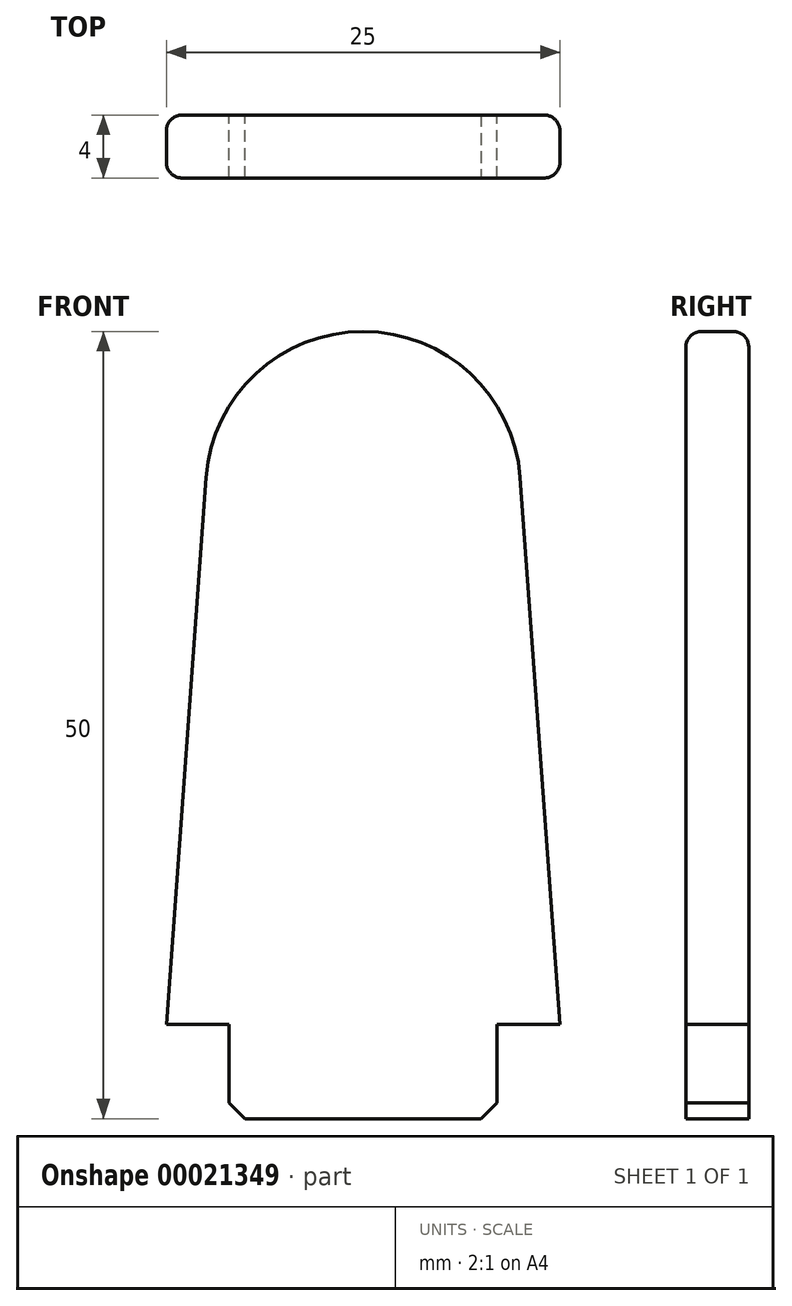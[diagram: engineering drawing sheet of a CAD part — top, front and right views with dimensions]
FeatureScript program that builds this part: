
annotation { "Feature Type Name" : "Feature", "Feature Type Description" : "" }
export const myFeature = defineFeature(function(context is Context, id is Id, definition is map)
    precondition{}
    {
        {
            var Q0;
            Q0=qCreatedBy(makeId("Front.planeOp"),FACE);
            var sketch = newSketch(context, id + "F0", { "sketchPlane" : qUnion([Q0])});
            skLineSegment(sketch, "E0", {"start": v(0, 0) * mm, "end": v(0, 50) * mm});
            skLineSegment(sketch, "E1", {"start": v(0, 0) * mm, "end": v(8.5, 0) * mm});
            skLineSegment(sketch, "E2", {"start": v(8.5, 0) * mm, "end": v(8.5, 6) * mm});
            skLineSegment(sketch, "E3", {"start": v(8.5, 6) * mm, "end": v(12.5, 6) * mm});
            skLineSegment(sketch, "E4", {"start": v(12.5, 6) * mm, "end": v(9.97, 40.73) * mm});
            skArc(sketch, "E5", {"start": v(9.97, 40.73) * mm, "mid": v(6.8, 47.32) * mm, "end": v(0, 50) * mm});
            skLineSegment(sketch, "E6", {"start": v(0, 50) * mm, "end": v(-4.24, 50) * mm});
            skArc(sketch, "E7.MirrorCS", {"start": v(-9.97, 40.73) * mm, "mid": v(-6.8, 47.32) * mm, "end": v(0, 50) * mm});
            skLineSegment(sketch, "E8.MirrorCS", {"start": v(-12.5, 6) * mm, "end": v(-9.97, 40.73) * mm});
            skLineSegment(sketch, "E9.MirrorCS", {"start": v(-8.5, 6) * mm, "end": v(-12.5, 6) * mm});
            skLineSegment(sketch, "E10.MirrorCS", {"start": v(-8.5, 0) * mm, "end": v(-8.5, 6) * mm});
            skLineSegment(sketch, "E11.MirrorCS", {"start": v(0, 0) * mm, "end": v(-8.5, 0) * mm});
            skSolve(sketch);
        }
        {
            var Q0;
            Q0=makeQuery(id+"F0.imprint","IMPRINT",FACE,{"disambiguationData":[TD([[makeQuery(id+"F0.imprint","IMPRINT",EDGE,{"derivedFrom":sQuery(id+"F0.wireOp",EDGE,"E0")}),1.0]])]});
            var Q1;
            Q1=makeQuery(id+"F0.imprint","IMPRINT",FACE,{"disambiguationData":[TD([[makeQuery(id+"F0.imprint","IMPRINT",EDGE,{"derivedFrom":sQuery(id+"F0.wireOp",EDGE,"E0")}),-1.0]])]});
            extrude(context, id + "F1", {"entities" : qUnion([Q0, Q1]), "endBound" : BoundingType.SYMMETRIC, "depth" : 4 * mm});
        }
        {
            var Q0;
            Q0=makeQuery(id+"F1.opExtrude","CAP_EDGE",EDGE,{"disambiguationData":[OSD([sQuery(id+"F0.wireOp",EDGE,"E8.MirrorCS")])],"isStart":false});
            var Q1;
            Q1=makeQuery(id+"F1.opExtrude","CAP_EDGE",EDGE,{"disambiguationData":[OSD([sQuery(id+"F0.wireOp",EDGE,"E5"),sQuery(id+"F0.wireOp",EDGE,"E7.MirrorCS")])],"isStart":false});
            var Q2;
            Q2=makeQuery(id+"F1.opExtrude","CAP_EDGE",EDGE,{"disambiguationData":[OSD([sQuery(id+"F0.wireOp",EDGE,"E4")])],"isStart":false});
            var Q3;
            Q3=makeQuery(id+"F1.opExtrude","CAP_EDGE",EDGE,{"disambiguationData":[OSD([sQuery(id+"F0.wireOp",EDGE,"E5"),sQuery(id+"F0.wireOp",EDGE,"E7.MirrorCS")])],"isStart":true});
            var Q4;
            Q4=makeQuery(id+"F1.opExtrude","CAP_EDGE",EDGE,{"disambiguationData":[OSD([sQuery(id+"F0.wireOp",EDGE,"E8.MirrorCS")])],"isStart":true});
            var Q5;
            Q5=makeQuery(id+"F1.opExtrude","CAP_EDGE",EDGE,{"disambiguationData":[OSD([sQuery(id+"F0.wireOp",EDGE,"E4")])],"isStart":true});
            fillet(context, id + "F2", {"entities" : qUnion([Q0, Q1, Q2, Q3, Q4, Q5]), "radius" : 1 * mm, "tangentPropagation" : true, "allowEdgeOverflow" : false});
        }
        {
            var Q0;
            Q0=makeQuery(id+"F1.opExtrude","SWEPT_EDGE",EDGE,{"disambiguationData":[OSD([sQuery(id+"F0.wireOp",EDGE,"E1"),sQuery(id+"F0.wireOp",EDGE,"E2")])]});
            var Q1;
            Q1=makeQuery(id+"F1.opExtrude","SWEPT_EDGE",EDGE,{"disambiguationData":[OSD([sQuery(id+"F0.wireOp",EDGE,"E10.MirrorCS"),sQuery(id+"F0.wireOp",EDGE,"E11.MirrorCS")])]});
            chamfer(context, id + "F3", {"entities" : qUnion([Q0, Q1]), "width" : 1 * mm, "tangentPropagation" : true});
        }
    });
